# Revit family: CSP_Ver.2.5
name_source: partatom
category: Windows
revit_build: Autodesk Revit Architecture 2014 (Build: 20130308_1515(x64)
units: mm (PartAtom-declared; Revit-internal decimal feet)

## types (2) — shared parameters
2d details = http://www.velux.co.uk
AcousticRating = 33
Air permeability Class = 4
Allowed Roof Slope = 0°-15°
Assembly Code = B3020110
Colour = Acrylic/PVC Color NCS S 0502-Y
Count = 1
Cross Height = 85.657 mm
Description = http://www.velux.co.uk
Disclaimer = When installing VELUX roof windows the costumer must make sure to meet local applicable building and fire requirements. VELUX shall not be liable for the objects/drawings and the constructional quality of the installation. Please contact VELUX for technical specifications of VELUX roof windows, flashings, installations products and internal/external accessories.
Documentation = http://www.professional.velux.co.uk
Emergency Exit = No
Features = Smoke ventilation flat roof window
Finish = PVC Color NCS S 0502-Y
FireRating = E
Function = Smoke ventilation flat roof window
Glazing = 73FQT + ISD 0000
Installation instructions = http://www.velux.co.uk roof windows
IsExternal = Yes
Light transmittance = 0.72
Manufacturer = VELUX A/S
Manufacturer URL = www.VELUX.com/ce
Material = Acrylic/PVC Color NCS S 0502-Y
Material External = Acrylic/PVC Color NCS S 0502-Y
Material Internal = PVC Color NCS S 0502-Y
Model = Flat roof window - CSP
Offset from Roof = 600 mm  [stored 1.9685 ft]
Open Window = No
Opening = 159.38 mm  [stored 0.5229 ft]
Opening Lines = Yes
Operation Mode = 0
Product certification = www.velux.com/ce
ReferenceStandard = www.velux.com/ce
SmokeStop = No
Sound Insulation db = 33
Technical description = http://www.velux.co.uk
Thermal Resistance (R) = 1
ThermalBridge(Installation) W/mK = 0.05
ThermalTransmittance = 1
URL = www.velux.com
Ultraviolet Transmittance = 0.05
Warranty Years = 10
Water Tightness Class = Passed
Within Standard Sizes = Yes
g-value = 0.53
zero-valued in all types: Placement Height, Rough Height, Rough Width

## per-type parameters (varying)
| type | Aerodynamic free area Aa (m2) | Dome Profile Length | Half Height | Half Width | Height | Height Dome | NominalHeight | NominalWidth | PerimeterWindow m | Width | Width Dome |
| CSP size 1000x1000 (100100) | 0.42 | 587.49 mm | 587.49 mm | 587.49 mm | 1180 mm | 1000 mm  [stored 3.28084 ft] | 1180 | 1180 | 4 | 1180 mm | 1000 mm  [stored 3.28084 ft] |
| CSP size 1200x1200 (120120) | 0.58 | 687.49 mm | 687.49 mm | 687.49 mm | 1380 mm  [stored 4.52756 ft] | 1200 mm | 1380 | 1380 | 4.8 | 1380 mm  [stored 4.52756 ft] | 1200 mm |

note: column(s) folded — value = type name in every type: ModelReference, Size

note: [stored X ft] marks values corroborated as IEEE doubles in the binary element streams (Revit-internal decimal feet)

## geometry (parser evidence)
native form markers: Blend x17, Sweep x3
no freeform markers — native parametric forms only
